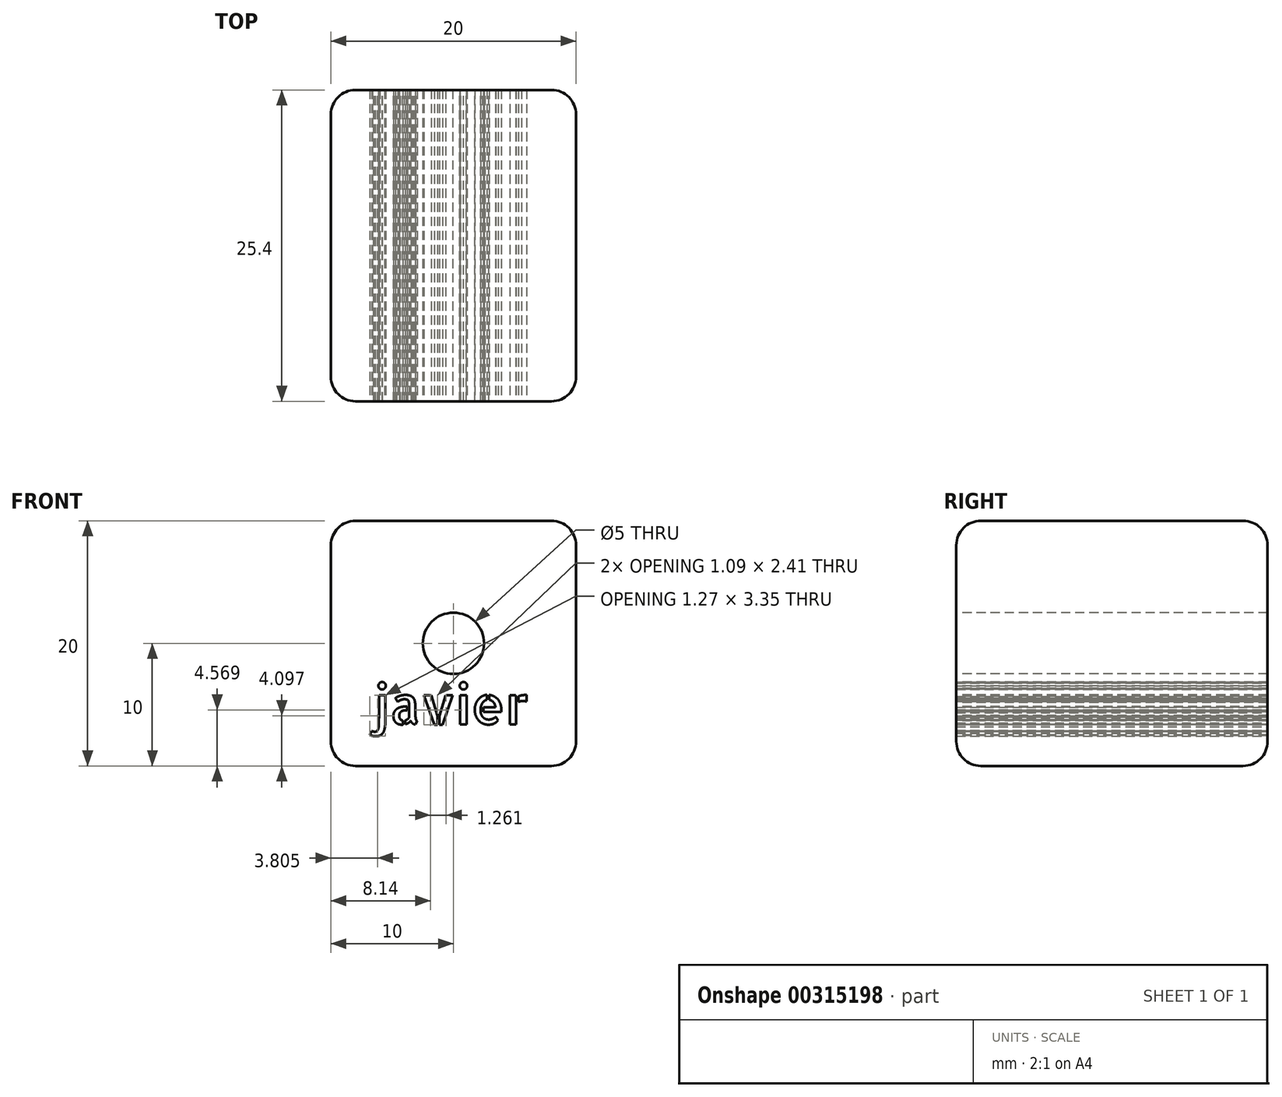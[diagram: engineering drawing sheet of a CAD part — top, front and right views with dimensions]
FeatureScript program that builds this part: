
annotation { "Feature Type Name" : "Feature", "Feature Type Description" : "" }
export const myFeature = defineFeature(function(context is Context, id is Id, definition is map)
    precondition{}
    {
        {
            var Q0;
            Q0=qCreatedBy(makeId("Front.planeOp"),FACE);
            var sketch = newSketch(context, id + "F0", { "sketchPlane" : qUnion([Q0])});
            skLineSegment(sketch, "E0.bottom", {"start": v(10, 10) * mm, "end": v(-10, 10) * mm});
            skLineSegment(sketch, "E0.top", {"start": v(10, -10) * mm, "end": v(-10, -10) * mm});
            skLineSegment(sketch, "E0.left", {"start": v(10, 10) * mm, "end": v(10, -10) * mm});
            skLineSegment(sketch, "E0.right", {"start": v(-10, 10) * mm, "end": v(-10, -10) * mm});
            skPoint(sketch, "E0.middle", {"position": v(0, 0) * mm});
            skSolve(sketch);
        }
        {
            var Q0;
            Q0 = qSketchRegion(id + "F0", true);
            extrude(context, id + "F1", {"entities" : qUnion([Q0]), "depth" : 25.4 * mm});
        }
        {
            var Q0;
            Q0=makeQuery(id+"F1.opExtrude","CAP_FACE",FACE,{"disambiguationData":[OSD([sQuery(id+"F0.wireOp",EDGE,"E0.bottom"),sQuery(id+"F0.wireOp",EDGE,"E0.top"),sQuery(id+"F0.wireOp",EDGE,"E0.left"),sQuery(id+"F0.wireOp",EDGE,"E0.right")])],"isStart":false});
            var sketch = newSketch(context, id + "F2", { "sketchPlane" : qUnion([Q0])});
            skCircle(sketch, "E1", {"center": v(0, 0) * mm, "radius": 2.5 * mm});
            skSolve(sketch);
        }
        {
            var Q0;
            Q0 = qSketchRegion(id + "F2", true);
            extrude(context, id + "F3", {"entities" : qUnion([Q0]), "operationType" : NewBodyOperationType.REMOVE, "oppositeDirection" : true, "depth" : 34.67 * mm});
        }
        {
            var Q0;
            Q0=makeQuery(id+"F1.opExtrude","CAP_EDGE",EDGE,{"disambiguationData":[OSD([sQuery(id+"F0.wireOp",EDGE,"E0.right")])],"isStart":false});
            var Q1;
            Q1=makeQuery(id+"F1.opExtrude","CAP_EDGE",EDGE,{"disambiguationData":[OSD([sQuery(id+"F0.wireOp",EDGE,"E0.top")])],"isStart":false});
            var Q2;
            Q2=makeQuery(id+"F1.opExtrude","CAP_EDGE",EDGE,{"disambiguationData":[OSD([sQuery(id+"F0.wireOp",EDGE,"E0.bottom")])],"isStart":false});
            var Q3;
            Q3=makeQuery(id+"F1.opExtrude","CAP_EDGE",EDGE,{"disambiguationData":[OSD([sQuery(id+"F0.wireOp",EDGE,"E0.left")])],"isStart":false});
            var Q4;
            Q4=makeQuery(id+"F1.opExtrude","SWEPT_FACE",FACE,{"disambiguationData":[OSD([sQuery(id+"F0.wireOp",EDGE,"E0.right")])]});
            var Q5;
            Q5=makeQuery(id+"F1.opExtrude","CAP_EDGE",EDGE,{"disambiguationData":[OSD([sQuery(id+"F0.wireOp",EDGE,"E0.top")])],"isStart":true});
            var Q6;
            Q6=makeQuery(id+"F1.opExtrude","SWEPT_EDGE",EDGE,{"disambiguationData":[OSD([sQuery(id+"F0.wireOp",EDGE,"E0.top"),sQuery(id+"F0.wireOp",EDGE,"E0.left")])]});
            var Q7;
            Q7=makeQuery(id+"F1.opExtrude","SWEPT_EDGE",EDGE,{"disambiguationData":[OSD([sQuery(id+"F0.wireOp",EDGE,"E0.bottom"),sQuery(id+"F0.wireOp",EDGE,"E0.left")])]});
            var Q8;
            Q8=makeQuery(id+"F1.opExtrude","CAP_EDGE",EDGE,{"disambiguationData":[OSD([sQuery(id+"F0.wireOp",EDGE,"E0.bottom")])],"isStart":true});
            var Q9;
            Q9=makeQuery(id+"F1.opExtrude","CAP_EDGE",EDGE,{"disambiguationData":[OSD([sQuery(id+"F0.wireOp",EDGE,"E0.left")])],"isStart":true});
            fillet(context, id + "F4", {"entities" : qUnion([Q0, Q1, Q2, Q3, Q4, Q5, Q6, Q7, Q8, Q9]), "radius" : 2 * mm, "tangentPropagation" : true, "allowEdgeOverflow" : false});
        }
        {
            var Q0;
            Q0=makeQuery(id+"F1.opExtrude","CAP_FACE",FACE,{"disambiguationData":[OSD([sQuery(id+"F0.wireOp",EDGE,"E0.bottom"),sQuery(id+"F0.wireOp",EDGE,"E0.top"),sQuery(id+"F0.wireOp",EDGE,"E0.left"),sQuery(id+"F0.wireOp",EDGE,"E0.right")])],"isStart":false});
            var sketch = newSketch(context, id + "F5", { "sketchPlane" : qUnion([Q0])});
            skText(sketch, "E2", { "text": "javier", "fontName": "AllertaStencil-Regular.ttf"});
            const initialGuessF5  = {"E2": [-0.00659, -0.00662, 1, 0, 0.00313]};
            skSetInitialGuess(sketch, initialGuessF5);
            skSolve(sketch);
        }
        {
            var Q0;
            Q0 = qSketchRegion(id + "F5", true);
            extrude(context, id + "F6", {"entities" : qUnion([Q0]), "operationType" : NewBodyOperationType.REMOVE, "oppositeDirection" : true, "depth" : 36.32 * mm});
        }
    });
